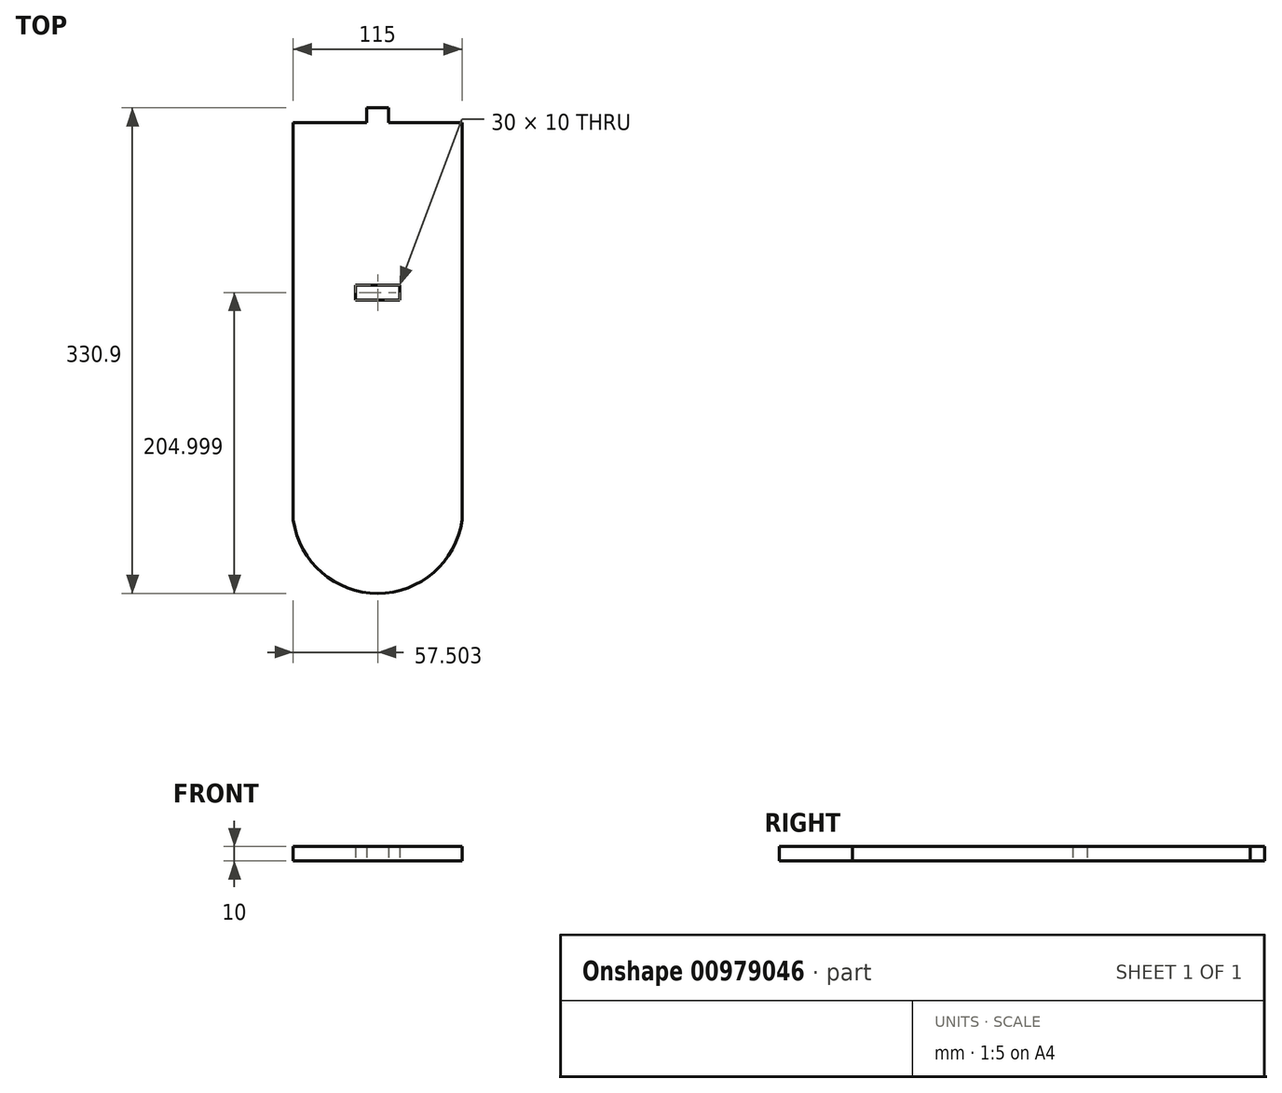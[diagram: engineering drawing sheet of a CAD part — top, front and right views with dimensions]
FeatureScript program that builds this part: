
annotation { "Feature Type Name" : "Feature", "Feature Type Description" : "" }
export const myFeature = defineFeature(function(context is Context, id is Id, definition is map)
    precondition{}
    {
        {
            var Q0;
            Q0=qCreatedBy(makeId("Top.planeOp"),FACE);
            var sketch = newSketch(context, id + "F0", { "sketchPlane" : qUnion([Q0])});
            skLineSegment(sketch, "E0.left", {"start": v(107.92, 37.17) * mm, "end": v(107.92, -233.73) * mm});
            skLineSegment(sketch, "E0.right", {"start": v(222.92, 37.17) * mm, "end": v(222.92, -233.73) * mm});
            skLineSegment(sketch, "E1", {"start": v(107.92, 37.17) * mm, "end": v(157.92, 37.17) * mm});
            skLineSegment(sketch, "E2", {"start": v(157.92, 37.17) * mm, "end": v(157.92, 47.17) * mm});
            skLineSegment(sketch, "E3", {"start": v(157.92, 47.17) * mm, "end": v(172.92, 47.17) * mm});
            skLineSegment(sketch, "E4", {"start": v(172.92, 47.17) * mm, "end": v(172.92, 37.17) * mm});
            skLineSegment(sketch, "E5", {"start": v(172.92, 37.17) * mm, "end": v(222.92, 37.17) * mm});
            skLineSegment(sketch, "E6.bottom", {"start": v(150.42, -73.73) * mm, "end": v(180.42, -73.73) * mm});
            skLineSegment(sketch, "E6.top", {"start": v(150.42, -83.73) * mm, "end": v(180.42, -83.73) * mm});
            skLineSegment(sketch, "E6.left", {"start": v(150.42, -73.73) * mm, "end": v(150.42, -83.73) * mm});
            skLineSegment(sketch, "E6.right", {"start": v(180.42, -73.73) * mm, "end": v(180.42, -83.73) * mm});
            skArc(sketch, "E7", {"start": v(107.92, -233.73) * mm, "mid": v(165.42, -283.73) * mm, "end": v(222.92, -233.73) * mm});
            skSolve(sketch);
        }
        {
            var Q0;
            Q0=makeQuery(id+"F0.imprint","IMPRINT",FACE,{"disambiguationData":[TD([[makeQuery(id+"F0.imprint","IMPRINT",EDGE,{"derivedFrom":sQuery(id+"F0.wireOp",EDGE,"E0.left")}),1.0]])]});
            extrude(context, id + "F1", {"entities" : qUnion([Q0]), "depth" : 10 * mm, "offsetDistance" : 25 * mm});
        }
    });
